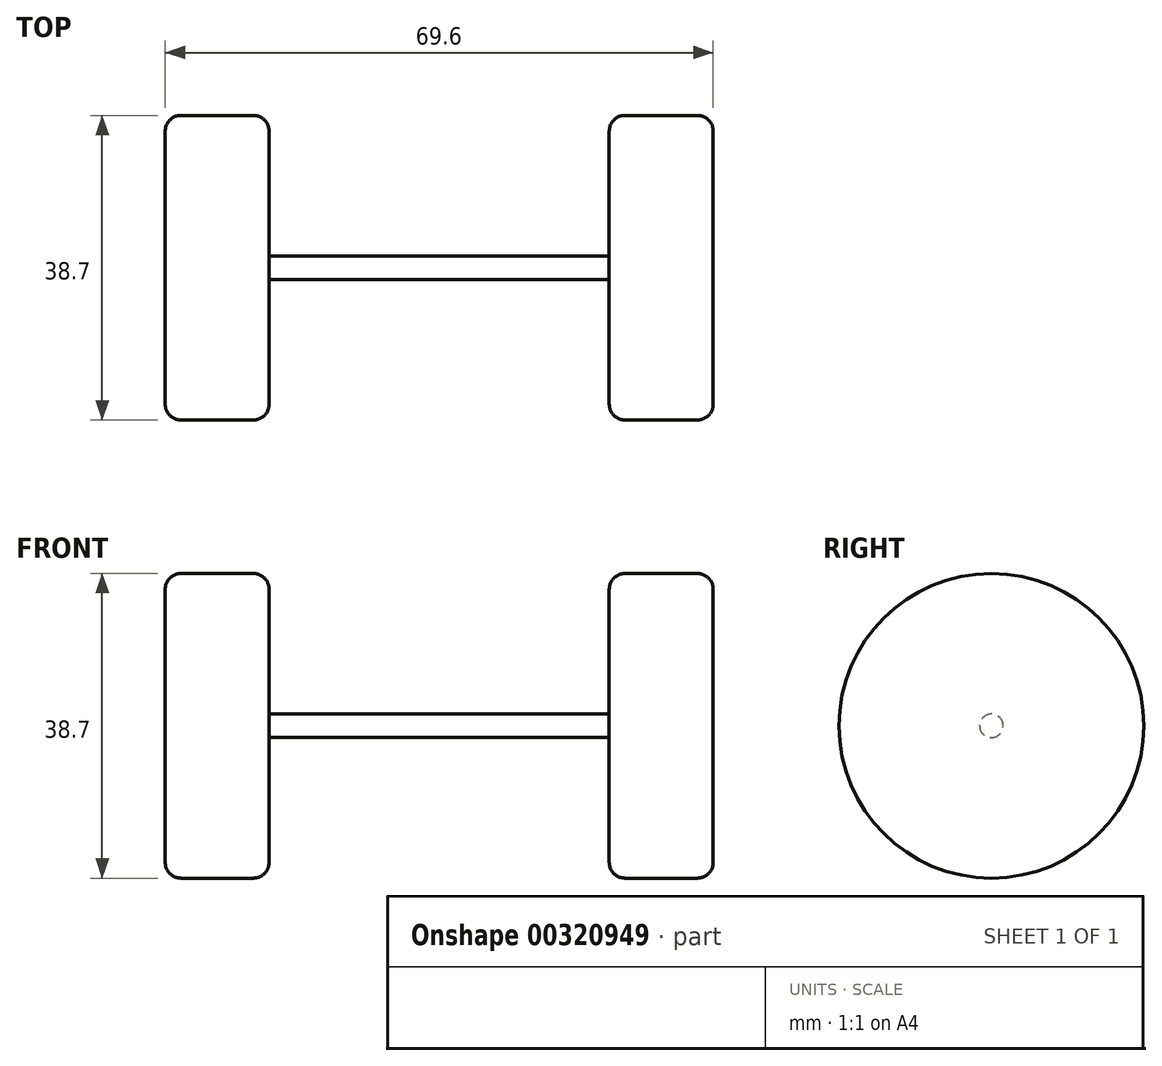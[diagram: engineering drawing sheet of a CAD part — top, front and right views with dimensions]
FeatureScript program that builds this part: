
annotation { "Feature Type Name" : "Feature", "Feature Type Description" : "" }
export const myFeature = defineFeature(function(context is Context, id is Id, definition is map)
    precondition{}
    {
        {
            var Q0;
            Q0=qCreatedBy(makeId("Right.planeOp"),FACE);
            var sketch = newSketch(context, id + "F0", { "sketchPlane" : qUnion([Q0])});
            skCircle(sketch, "E0", {"center": v(0, 0) * mm, "radius": 19.35 * mm});
            skSolve(sketch);
        }
        {
            var Q0;
            Q0 = qSketchRegion(id + "F0", true);
            extrude(context, id + "F1", {"entities" : qUnion([Q0]), "depth" : 13.2 * mm});
        }
        {
            var Q0;
            Q0=makeQuery(id+"F1.opExtrude","CAP_FACE",FACE,{"disambiguationData":[OSD([sQuery(id+"F0.wireOp",EDGE,"E0")])],"isStart":false});
            var sketch = newSketch(context, id + "F2", { "sketchPlane" : qUnion([Q0])});
            skCircle(sketch, "E1", {"center": v(0, 0) * mm, "radius": 1.5 * mm});
            skSolve(sketch);
        }
        {
            var Q0;
            Q0 = qSketchRegion(id + "F2", true);
            extrude(context, id + "F3", {"entities" : qUnion([Q0]), "operationType" : NewBodyOperationType.ADD, "depth" : 43.2 * mm});
        }
        {
            var Q0;
            Q0=makeQuery(id+"F3.opExtrude","CAP_FACE",FACE,{"disambiguationData":[OSD([sQuery(id+"F2.wireOp",EDGE,"E1")])],"isStart":false});
            var sketch = newSketch(context, id + "F4", { "sketchPlane" : qUnion([Q0])});
            skCircle(sketch, "E2", {"center": v(0, 0) * mm, "radius": 19.35 * mm});
            skSolve(sketch);
        }
        {
            var Q0;
            Q0 = qSketchRegion(id + "F4", true);
            extrude(context, id + "F5", {"entities" : qUnion([Q0]), "operationType" : NewBodyOperationType.ADD, "depth" : 13.2 * mm});
        }
        {
            var Q0;
            Q0=makeQuery(id+"F1.opExtrude","CAP_EDGE",EDGE,{"disambiguationData":[OSD([sQuery(id+"F0.wireOp",EDGE,"E0")])],"isStart":true});
            var Q1;
            Q1=makeQuery(id+"F1.opExtrude","CAP_EDGE",EDGE,{"disambiguationData":[OSD([sQuery(id+"F0.wireOp",EDGE,"E0")])],"isStart":false});
            var Q2;
            Q2=makeQuery(id+"F5.opExtrude","CAP_EDGE",EDGE,{"disambiguationData":[OSD([sQuery(id+"F4.wireOp",EDGE,"E2")])],"isStart":true});
            var Q3;
            Q3=makeQuery(id+"F5.opExtrude","CAP_EDGE",EDGE,{"disambiguationData":[OSD([sQuery(id+"F4.wireOp",EDGE,"E2")])],"isStart":false});
            fillet(context, id + "F6", {"entities" : qUnion([Q0, Q1, Q2, Q3]), "radius" : 2 * mm, "tangentPropagation" : true, "allowEdgeOverflow" : false});
        }
    });
